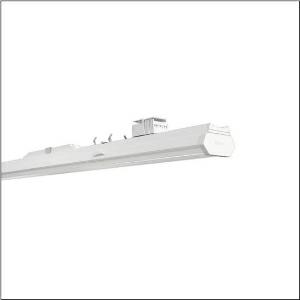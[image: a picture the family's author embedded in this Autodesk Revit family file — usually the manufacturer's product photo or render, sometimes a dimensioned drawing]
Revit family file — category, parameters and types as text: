
# Revit family: licross_r__11_protected_mo_51tp12cn58xf_fcc9
name_source: partatom
category: Lighting Fixtures
units: mm (PartAtom-declared; Revit-internal decimal feet)

## family parameters
Cut with Voids When Loaded = No
Host = Face
Light Source = No
Part Type = Normal
Room Calculation Point = No
Round Connector Dimension = Use Diameter
Shared = No

## types (1)
- --- (1 x LED, 8190 lm, 49 W, 5000K)
    Apparent Load = 49 VA
    CIE Flux Codes = 73 92 98 99 100
    Color Rendering = 80
    Color Temperature = 5000K
    Default Elevation = 1800 mm
    Description = Licross® 11 Protected MO, luminaire insert, of sheet steel, galvanised, coil coated, white, length: 1.500mm, width: 90mm, height: 101mm, LED rated luminous flux: 8.190lm, light colour: 850, control gear: ON/OFF Multilumen, CLOi, control gear: ECG Multilumen, with plug, 3-pole, with phase selection, mains connection: 220..240V, AC, 50/60Hz, start of lifetime: 49W, end of service life: 54W, internal wiring halogen-free, primary optical cover: cover, of PMMA, light emission: direct distribution, primary light characteristic: symmetric, protection rating (complete): IP64, insulation class (complete): insulation class I (protective earthing), certification: CE, ENEC, VDE, UKCA, protection symbol: D if used in an environment with conductive dust loads with corresponding accessories, impact resistance: IK06, permissible ambient temperature for indoor applications: -35..+40°C, reducing of maximum allowable ambient temperature of 5°C with ceiling mounting, corresponds to IFS (International Featured Standards) requirements for safety and quality in the food industry, LABS conformity tested according to VDMA 24364:2018-05, packaging unit: 1 piece
    Height = 92 mm
    Lamp = 1 x LED
    Lamp Light Flux = 8190 lm
    Lamp Power = 49 W
    Lamp count = 1
    Length = 1500 mm
    Luminous efficacy = 167 lm/W
    Manufacturer = Siteco
    ModVariant = No
    Model = 51TP12CN58XF
    Mounting Place = Ceiling
    Mounting Type = Pendant
    Number of Poles = 1
    OnlyDefault = Yes
    Power Factor = 1
    Product Name = Licross® 11 Protected MO
    Product group = luminaire insert | ceiling pendant
    ProductGroupID = 902
    Protection Class = Protection class I
    Protection Degree = IP 64
    RLX_Detail_Level = 1
    RLX_Emergency_Light_Flux = 0 lm
    RLX_Emergency_Type = 0
    RLX_Emergency_Type_DB = No
    RlxData = <blob elided: 21993 chars, md5=7382a137>
    Socket = socket
    Standby Power = 0 W
    System Light Flux = 8190 lm
    System Power = 49 W
    Type Comments = factory setting: luminous flux: 100 % | (A | C | E) | 111 mA
    Type Image = l_1256148.jpg
    URL = http://relux.com
    VarID = @adj_219783
    Voltage = 0 V
    Weight = 0.00 kg
    Width = 88 mm

## geometry (parser evidence)
native form markers: Blend x4, Sweep x11
no freeform markers — native parametric forms only
